# Revit family: QF_ELECTROLUXPROFESSIONAL_727251_ESP71FRR
name_source: partatom
category: Attrezzature speciali
units: mm (PartAtom-declared; Revit-internal decimal feet)

## family parameters
Basato su piano di lavoro = No
Condiviso = No
Punto di calcolo locali = No
Quota connettore circolare = Usa diametro
Sempre verticale = Sì
Taglio con vuoti quando caricato = No
Tipo di parte = Normale

## types (1)
- Standard
    Accessory = Sì
    Cold Water Size = 0 mm
    Compressed Air Pressure = 0.0 Pa
    Compressed Air Size = 0 mm
    Compressed Air Volume = 0.0 L/s
    Condensate Return Size = 0 mm
    Cycle = 50 Hz
    Depth Actual = 835 mm
    Descrizione = 1-DOOR REFRIGERATOR 670L -2/+10°C, DIGITAL, REM
    Direct Waste Size = 0 mm
    Gas Input Pressure = 0
    Gas KW = 0
    Gas Size = 0 mm
    HP = 0.4 HP
    Height Actual = 2050 mm  [stored 6.72572 ft]
    Hot Water Size = 0 mm
    Item Number = 727251
    Length Actual = 710 mm
    Modello = ESP71FRR
    Phase = 1
    Produttore = Electrolux Professional
    Prospetto di default = 0 mm  [stored 0 ft]
    Refrigerant Compressor Remote = Sì
    Refrigeration Liquid Line Size = 6 mm  [stored 0.019685 ft]
    Refrigeration Suction Line Size = 10 mm  [stored 0.0328084 ft]
    Steam Consumption per Hour = 0
    Steam Supply Maximum Pressure = 0.0 Pa
    Steam Supply Minimum Pressure = 0.0 Pa
    Steam Supply Size = 0 mm
    URL = https://www.electroluxprofessional.com
    URL Manufacturer = https://www.electroluxprofessional.com
    Volts = 220 V
    Watts = 305 W
    Weight = 102.00 kg

note: source unit labels omitted for Gas Input Pressure — the stored unit's dimension contradicts the parameter name (converter mislabeling)

note: [stored X ft] marks values corroborated as IEEE doubles in the binary element streams (Revit-internal decimal feet)

## geometry (parser evidence)
native form markers: Sweep x2
no freeform markers — native parametric forms only
